# Revit family: 343900xx1--High WC cistern without cover-Universal-343900xx1
name_source: partatom
category: Plumbing Fixtures
units: mm (PartAtom-declared; Revit-internal decimal feet)

## family parameters
Always vertical = Yes
Cut with Voids When Loaded = No
Host = Wall
OmniClass Number = 23.45.05.00
OmniClass Title = Sanitary Equipment
Part Type = Normal
Room Calculation Point = No
Round Connector Dimension = Use Diameter
Shared = No

## types (1)
- 343900001-White
    Description = High WC cistern without cover
    Drain Diameter = 45 mm  [stored 0.147638 ft]
    Height = 275 mm
    Length = 370 mm
    Manufacturer URL = www.roca.com
    Manufacturer name = Roca
    Model = 343900..1
    Primary Material = White - Universal - Roca
    Product SKU = 343900xx1
    QR code = https://www.roca.com
    URL = http://www.export.roca.com
    Water Inlet Diameter = 13 mm
    Width = 210 mm

note: [stored X ft] marks values corroborated as IEEE doubles in the binary element streams (Revit-internal decimal feet)

## geometry (parser evidence)
native form markers: Blend x4, Sweep x4
no freeform markers — native parametric forms only
